# Revit family: Volta-IP30-Hollow_wall-leer-NoHosted-AT-de
name_source: partatom
category: Electrical Equipment
units: mm (PartAtom-declared; Revit-internal decimal feet)

## family parameters
Always vertical = Yes
Cut with Voids When Loaded = No
Panel Configuration = Two Columns, Circuits Across
Part Type = Panelboard
Room Calculation Point = No
Round Connector Dimension = Use Diameter
Shared = No
Work Plane-Based = Yes

## types (10) — shared parameters
Default Elevation = 1219 mm
EF000003 - Montageart = EV000128 - Hohlwand
EF000007 - Farbe = EV000202 - weiß
EF000008 - Breite = 348 mm  [stored 1.14173 ft]
EF000049 - Tiefe = 98 mm  [stored 0.321522 ft]
EF000116 - RAL-Nummer = 9010
EF000118 - Mit Montageplatte = Yes
EF000218 - Einbautiefe = 89 mm  [stored 0.291995 ft]
EF000339 - Art der Abdeckung = EV004216 - Tür
EF000846 - Einbaubreite = 314 mm  [stored 1.03018 ft]
EF001062 - EMV-Ausführung = No
EF001088 - Anbaumöglichkeit = Yes
EF001131 - Innentiefe = 92 mm
EF001134 - DIN-Schiene = Yes
EF001596 - Werkstoff des Gehäuses = EV000154 - sonstige
EF002950 - Breite in Teilungseinheiten = 12
EF004462 - Art der Schließung = EV000154 - sonstige
EF005474 - Schutzart (IP) = EV006410 - IP30
EF006244 - Transparenter Deckel/Tür = No
EF006306 - Mit Schloss = No
EF009212 - Ausführung Deckel = EV009916 - mit Ausschnitt
EF015776 - Erdungsklemmenblock = No
EF015777 - Neutralleiterklemmenblock = No
EF015941 - Signaldurchlassende Tür = No
HG000002 - Mit tür = Yes
HG000003 - Bereich = Volta
HG000005 - Dicke = 3 mm  [stored 0.00984252 ft]
HG000006 - Unterputz = Yes
HG000009 - Doppelflügeligen Tür = No
HG000010 - Asymmetrische Türen = No
HG000011 - Leere Reihen von unten = No
Manufacturer = Hager
Type Comments = Volta
zero-valued in all types: EF000266 - Anzahl der Reihen, HG000001 - Anzahl der Spalten, HG000007 - Anzahl der leeren Spalten, HG000008 - Anzahl der leeren Reihen

## per-type parameters (varying)
| type | EF000040 - Höhe | EF000332 - Einbauhöhe | HG000004 - Herstellerreferenz | Model |
| Unterputz IP30 B348 H505.5 T98 12 Teilungseinheiten - VH24NWB | 506 mm | 470 mm | VH24NWB | VH24NWB |
| Unterputz IP30 B348 H630.5 T98 12 Teilungseinheiten - VH36NW | 630 mm | 595 mm | VH36NW | VH36NW |
| Unterputz IP30 B348 H630.5 T98 12 Teilungseinheiten - VH36NWB | 630 mm | 595 mm | VH36NWB | VH36NWB |
| Unterputz IP30 B348 H630.5 T98 12 Teilungseinheiten - VH36WWH | 630 mm | 595 mm | VH36WWH | VH36WWH |
| Unterputz IP30 B348 H755.5 T98 12 Teilungseinheiten - VH48NW | 756 mm | 720 mm | VH48NW | VH48NW |
| Unterputz IP30 B348 H755.5 T98 12 Teilungseinheiten - VH48NWB | 756 mm | 720 mm | VH48NWB | VH48NWB |
| Unterputz IP30 B348 H755.5 T98 12 Teilungseinheiten - VH48WWH | 756 mm | 720 mm | VH48WWH | VH48WWH |
| Unterputz IP30 B348 H880.5 T98 12 Teilungseinheiten - VH60NW | 880 mm  [stored 2.88714 ft] | 845 mm  [stored 2.77231 ft] | VH60NW | VH60NW |
| Unterputz IP30 B348 H880.5 T98 12 Teilungseinheiten - VH60NWB | 880 mm  [stored 2.88714 ft] | 845 mm  [stored 2.77231 ft] | VH60NWB | VH60NWB |
| Unterputz IP30 B348 H880.5 T98 12 Teilungseinheiten - VH60WWH | 880 mm  [stored 2.88714 ft] | 845 mm  [stored 2.77231 ft] | VH60WWH | VH60WWH |

note: [stored X ft] marks values corroborated as IEEE doubles in the binary element streams (Revit-internal decimal feet)

## geometry (parser evidence)
native form markers: Sweep x14
no freeform markers — native parametric forms only
